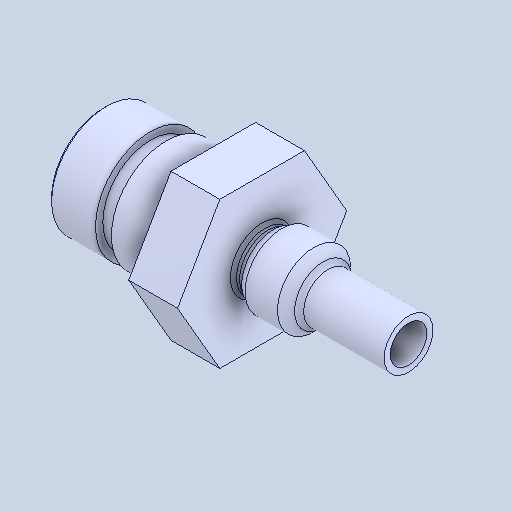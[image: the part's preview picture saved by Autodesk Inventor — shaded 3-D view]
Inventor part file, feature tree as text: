
AUTODESK INVENTOR PART (.ipt)
format: ipt  version: 2024.1 (Build 281209000, 209)  size: 161,280 bytes
history: native  units: in
note: dims shown in document units (in); Inventor stores cm internally (conversion verified against a paired STEP export)
features: chamfer x1
ambient origin geometry x8: Origin, YZ Plane, XZ Plane, XY Plane, X Axis, Y Axis, Z Axis, Center Point
bodies: Solid1 (feature_tree)
feature tree (1):
  chamfer  "Chamfer2"  [1 undecoded]
note: 1 required parameter value undecoded (feature->parameter linkage not recoverable at this tier; creation-order binding heuristic only, values carry confidence <= 0.55)
